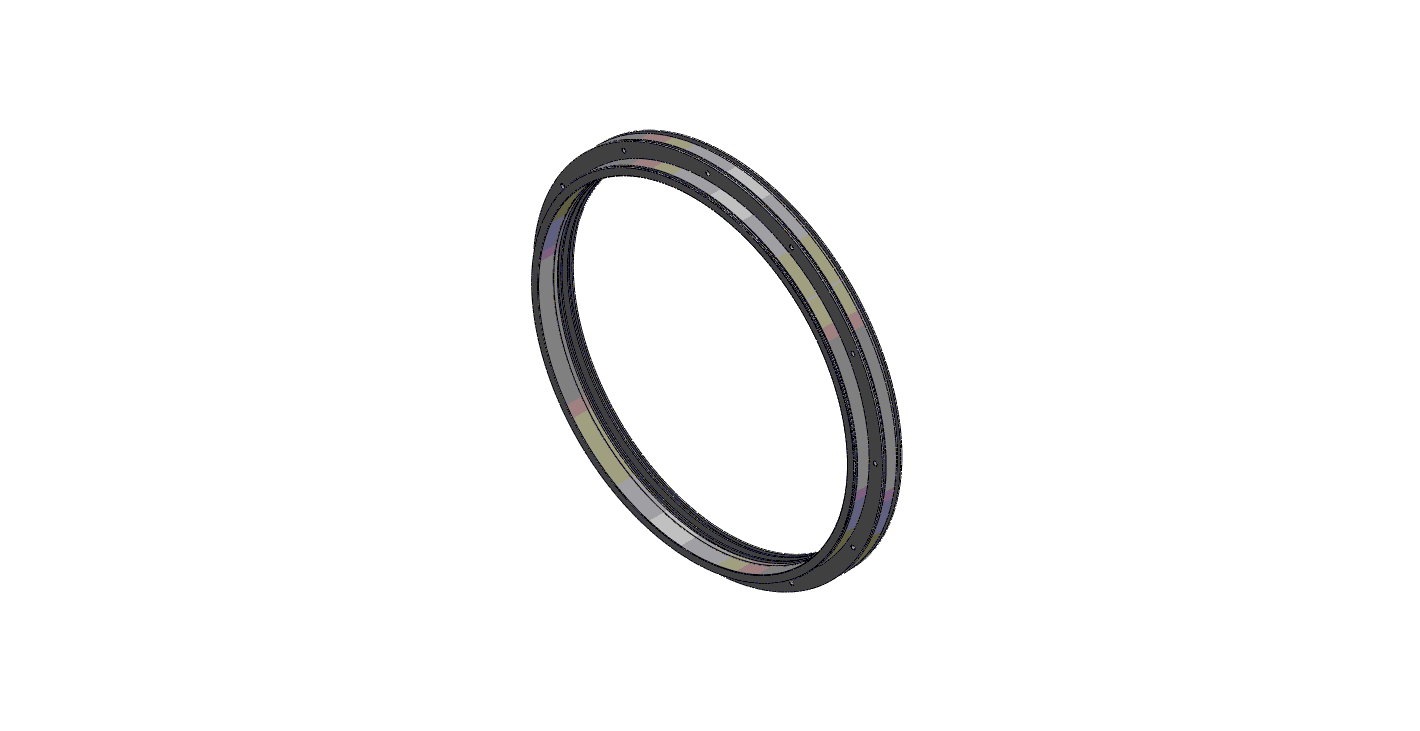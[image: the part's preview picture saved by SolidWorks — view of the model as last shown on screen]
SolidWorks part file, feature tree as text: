
SOLIDWORKS PART (.sldprt)
format: sldprt  version: not decoded by parser v0  size: 280,064 bytes
history: native  units: mm
features: sketch x4, plane x3, material x1, revolve x1, chamfer x1, hole x1, pattern_circular x1 (+8 scaffold rows collapsed)
feature tree (20):
  scaffold x8  (default folders/planes/origin — collapsed)
  material  "1.4401 (X5CrNiMo17-12-2)"
  plane  "Ebene vorne"
  plane  "Ebene oben"
  plane  "Ebene rechts"
  sketch  "Skizze1"  dims[c1.D1=5.0mm c1.D2=3.5mm c1.D3=10.0mm c1.D4=3.0mm c1.D5=3.0mm c1.D6=8.0mm c1.D7=13.0mm c1.D8=23.8mm c1.D9=1.0mm c1.D10=5.0mm c1.D11=3.5mm c1.D12=75.0mm c1.D13=14.0mm c1.D14=8.0mm c1.D15=6.3mm c1.D16=6.3mm c1.D17=30.0mm c1.D18=47.0mm c1.D19=38.0mm c1.D20=47.0mm c1.D21=83.5mm c1.D22=~54.178126mm c1.D23=33.0mm c1.D24=7.5mm c2.D22=419.0mm c2.D25=370.0mm c2.D23=387.5mm]
  revolve  "Rotation1"  Angle=360deg
  chamfer  "Fase1"  Distance=1mm Angle=45deg
  sketch  "Skizze2"  dims[D1=402.5mm]
  hole  "Bohrung1"  Diameter=20mm Depth=100mm
  sketch  "Skizze4"
  sketch  "Skizze3"  dims[Hole Ø=20.0mm Depth=100.0mm Drill Angle=118.0deg C.Sink Angle=90.0deg C.Bore Ø=40.0mm C.Bore Depth=20.0mm Durchmesser=9.0mm Tiefe=83.5mm Senkdurchmesser3=15.0mm Senktiefe1=9.0mm Spitzenwinkel=118.0deg]
  pattern_circular  "Kreismuster1"  Count=12 Angle=360deg
decode coverage: 7 of 8 modeling features carry decoded parameters
note: ~ marks probable driven/reference dimensions
note: suppression state not decoded; provenance and decode notes live in map.json
